# Revit family: Plumbing Fixture-Grease_Interseptor_Mifab_MI-G-SD
name_source: partatom
category: Plumbing Fixtures
revit_build: Autodesk Revit Structure 2013 (Build: 20120221_2030(x64)
units: mm (PartAtom-declared; Revit-internal decimal feet)

## types (8) — shared parameters
Description = Semi- Automatic Grease Interceptors with Draw Off Valve
Interceptor Material = Acid Resistant Epoxy Coated Green
Manufacturer = MIFAB
URL = www.mifab.com
zero-valued in all types: Default Elevation, WFU

## per-type parameters (varying)
| type | A | Assembly Code | B | C | D | E | F | Flow Rate | Grease Capacity | Standard Inlet And Outlet Radii | Water Capacity |
| MI-G-SD-1 | 17.75 " | D2090300 | 13.75 " | 3.5 " | 8.5 " | 12 " | 2 " | 7 GPM | 14 lbs | 1 " | 6 Gallons |
| MI-G-SD-2 | 21.25 " | D2090300 | 15.75 " | 3.5 " | 9.5 " | 13 " | 2 " | 10 GPM | 20 lbs | 1 " | 9.74 Gallons |
| MI-G-SD-3 | 23.75 " | D2090300 | 15.75 " | 3.5 " | 11.5 " | 15 " | 2 " | 15 GPM | 30 lbs | 1 " | 13.59 Gallons |
| MI-G-SD-4 | 23.75 " | D2090300 | 15.75 " | 3.5 " | 14 " | 17.5 " | 3 " | 20 GPM | 40 lbs | 1.5 " | 16.18 Gallons |
| MI-G-SD-5 | 27.75 " |  | 18.75 " | 3.5 " | 14 " | 17.5 " | 3 " | 25 GPM | 50 lbs | 1.5 " | 23.34 Gallons |
| MI-G-SD-6 | 31.25 " | D2090300 | 23.75 " | 5.5 " | 16.5 " | 22 " | 3 " | 35 GPM | 70 lbs | 1.5 " | 41.31 Gallons |
| MI-G-SD-7 | 31.25 " | D2090300 | 23.75 " | 5.5 " | 18.5 " | 24 " | 3 " | 50 GPM | 100 lbs | 1.5 " | 46.82 Gallons |
| MI-G-SD-8 | 42 " | D2090300 | 28 " | 6 " | 26 " | 32 " | 3 " | 75 GPM | 150 lbs | 1.5 " | 108.05 Gallons |

note: column(s) folded — value = type name in every type: Model

## geometry (parser evidence)
native form markers: Blend x5, Sweep x1
no freeform markers — native parametric forms only
